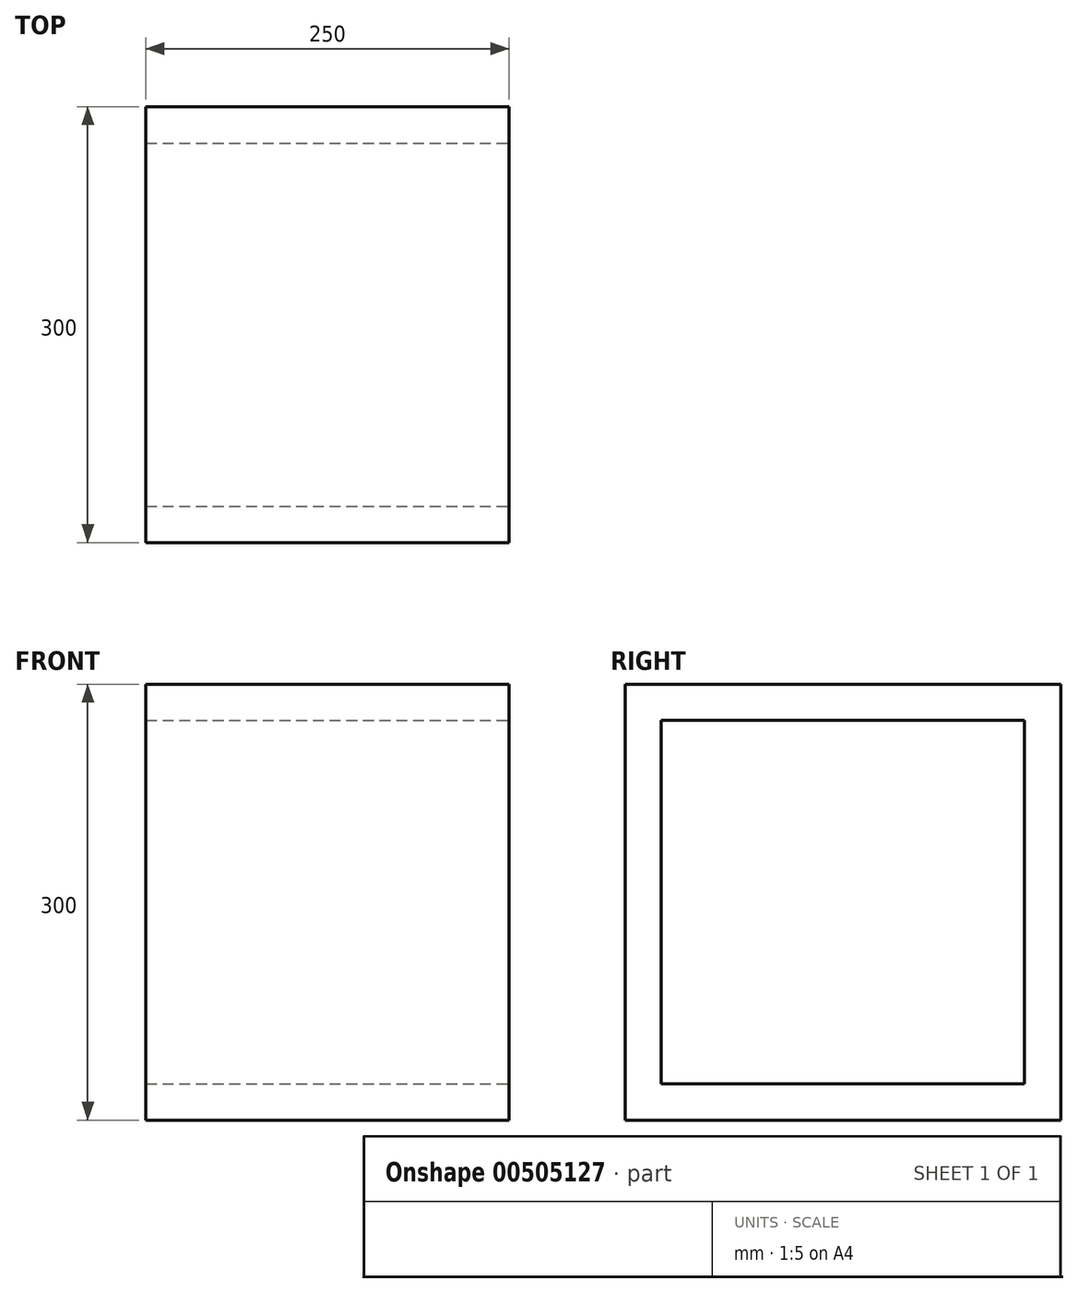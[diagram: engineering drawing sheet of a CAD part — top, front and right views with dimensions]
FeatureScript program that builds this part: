
annotation { "Feature Type Name" : "Feature", "Feature Type Description" : "" }
export const myFeature = defineFeature(function(context is Context, id is Id, definition is map)
    precondition{}
    {
        {
            var Q0;
            Q0=qCreatedBy(makeId("Front.planeOp"),FACE);
            var sketch = newSketch(context, id + "F0", { "sketchPlane" : qUnion([Q0])});
            skLineSegment(sketch, "E0.bottom", {"start": v(0, 0) * mm, "end": v(-250, 0) * mm});
            skLineSegment(sketch, "E0.top", {"start": v(0, 300) * mm, "end": v(-250, 300) * mm});
            skLineSegment(sketch, "E0.left", {"start": v(0, 0) * mm, "end": v(0, 300) * mm});
            skLineSegment(sketch, "E0.right", {"start": v(-250, 0) * mm, "end": v(-250, 300) * mm});
            skSolve(sketch);
        }
        {
            var Q0;
            Q0 = qSketchRegion(id + "F0", true);
            extrude(context, id + "F1", {"entities" : qUnion([Q0]), "depth" : 300 * mm});
        }
        {
            var Q0;
            Q0=makeQuery(id+"F1.opExtrude","SWEPT_FACE",FACE,{"disambiguationData":[OSD([sQuery(id+"F0.wireOp",EDGE,"E0.left")])]});
            var sketch = newSketch(context, id + "F2", { "sketchPlane" : qUnion([Q0])});
            skLineSegment(sketch, "E1.0", {"start": v(-275, 275) * mm, "end": v(-25, 275) * mm});
            skLineSegment(sketch, "E1.1", {"start": v(-275, 25) * mm, "end": v(-275, 275) * mm});
            skLineSegment(sketch, "E1.2", {"start": v(-275, 25) * mm, "end": v(-25, 25) * mm});
            skLineSegment(sketch, "E1.3", {"start": v(-25, 25) * mm, "end": v(-25, 275) * mm});
            skSolve(sketch);
        }
        {
            var Q0;
            Q0 = qSketchRegion(id + "F2", true);
            extrude(context, id + "F3", {"entities" : qUnion([Q0]), "operationType" : NewBodyOperationType.REMOVE, "endBound" : BoundingType.THROUGH_ALL, "oppositeDirection" : true, "depth" : 25 * mm});
        }
    });
